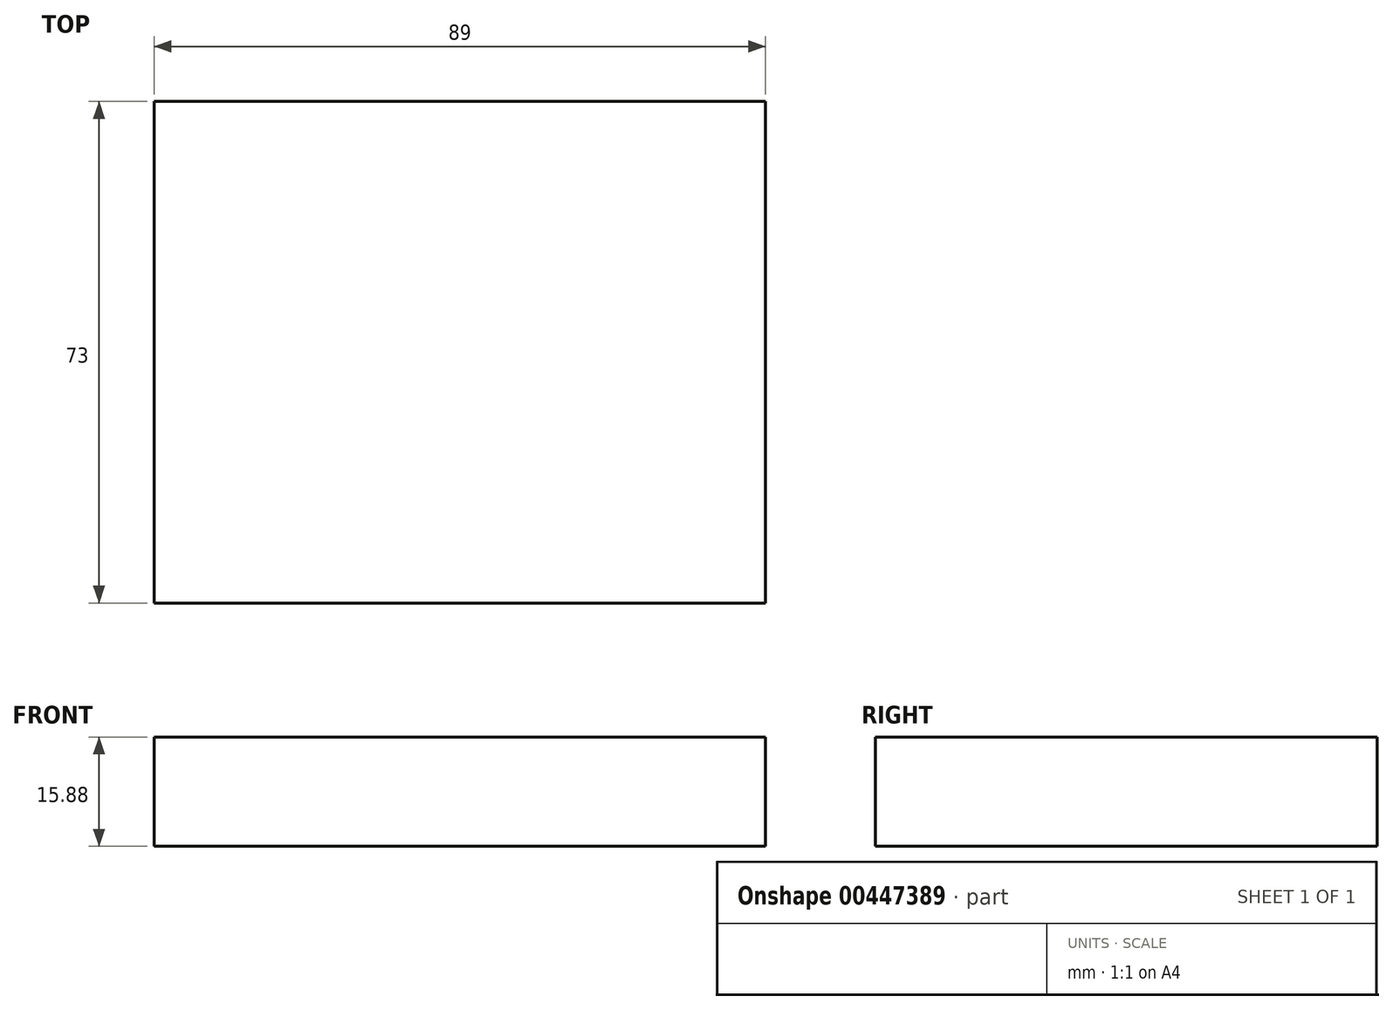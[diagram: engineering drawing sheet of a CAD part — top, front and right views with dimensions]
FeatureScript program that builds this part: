
annotation { "Feature Type Name" : "Feature", "Feature Type Description" : "" }
export const myFeature = defineFeature(function(context is Context, id is Id, definition is map)
    precondition{}
    {
        {
            var Q0;
            Q0=qCreatedBy(makeId("Front.planeOp"),FACE);
            var sketch = newSketch(context, id + "F0", { "sketchPlane" : qUnion([Q0])});
            skLineSegment(sketch, "E0.bottom", {"start": v(-38.71, 15.88) * mm, "end": v(50.3, 15.88) * mm});
            skLineSegment(sketch, "E0.top", {"start": v(-38.71, 0) * mm, "end": v(50.3, 0) * mm});
            skLineSegment(sketch, "E0.left", {"start": v(-38.71, 15.88) * mm, "end": v(-38.71, 0) * mm});
            skLineSegment(sketch, "E0.right", {"start": v(50.3, 15.88) * mm, "end": v(50.3, 0) * mm});
            skSolve(sketch);
        }
        {
            var Q0;
            Q0=makeQuery(id+"F0.imprint","IMPRINT",FACE,{"disambiguationData":[TD([[makeQuery(id+"F0.imprint","IMPRINT",EDGE,{"derivedFrom":sQuery(id+"F0.wireOp",EDGE,"E0.bottom")}),-1.0]])]});
            extrude(context, id + "F1", {"entities" : qUnion([Q0]), "depth" : 73 * mm});
        }
    });
